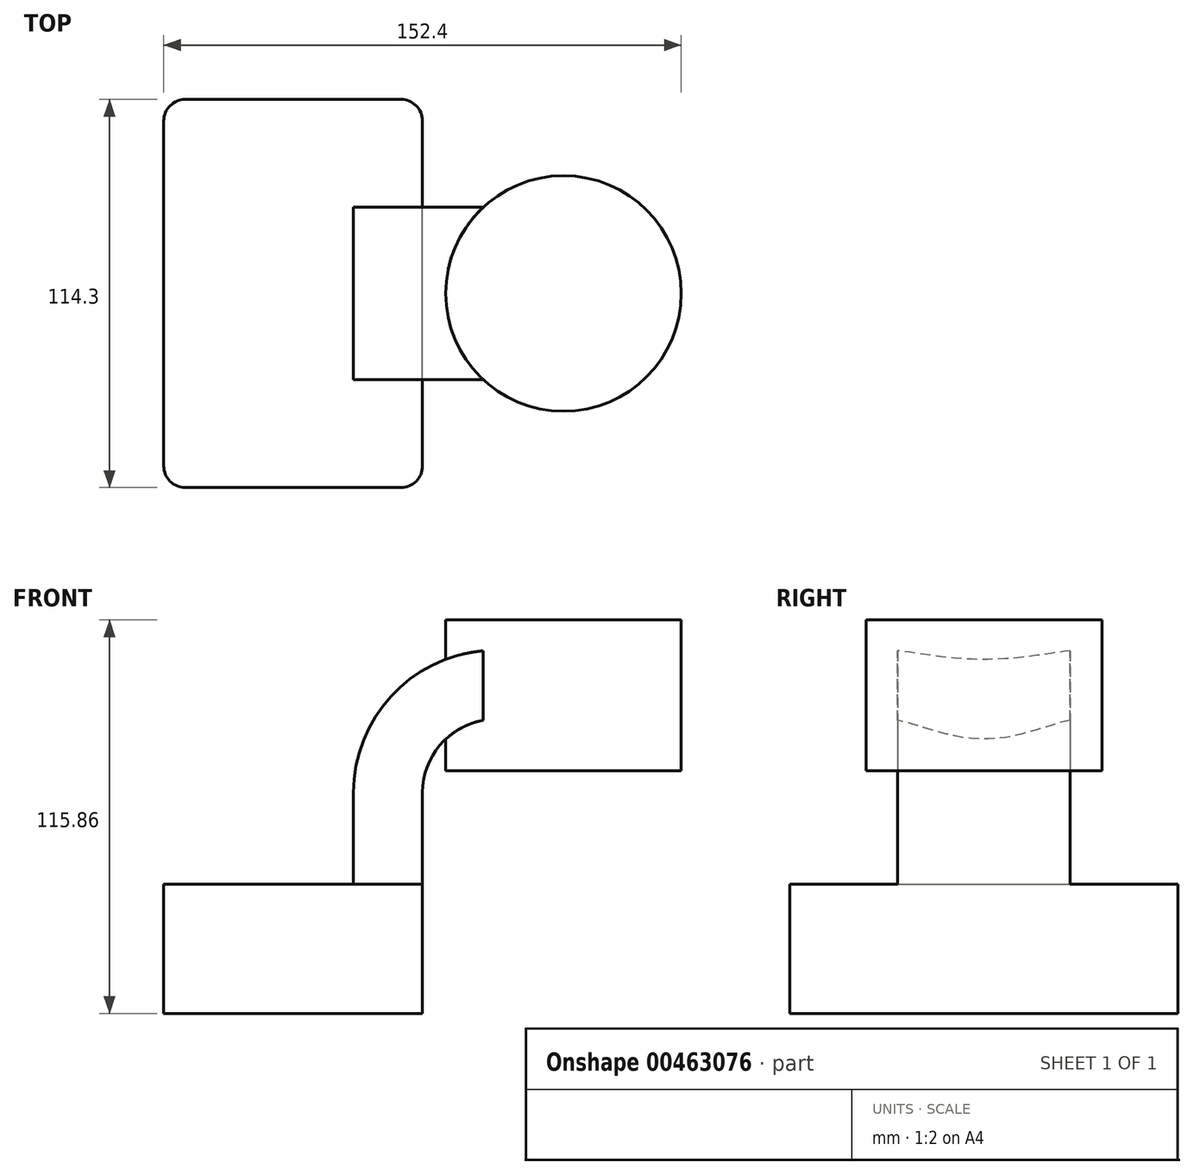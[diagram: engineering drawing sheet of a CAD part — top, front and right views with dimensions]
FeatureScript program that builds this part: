
annotation { "Feature Type Name" : "Feature", "Feature Type Description" : "" }
export const myFeature = defineFeature(function(context is Context, id is Id, definition is map)
    precondition{}
    {
        {
            var Q0;
            Q0=qCreatedBy(makeId("Front.planeOp"),FACE);
            var sketch = newSketch(context, id + "F0", { "sketchPlane" : qUnion([Q0])});
            skLineSegment(sketch, "E0.bottom", {"start": v(-34.93, -20.28) * mm, "end": v(41.27, -20.28) * mm});
            skLineSegment(sketch, "E0.top", {"start": v(-34.93, 17.82) * mm, "end": v(41.27, 17.82) * mm});
            skLineSegment(sketch, "E0.left", {"start": v(-34.93, -20.28) * mm, "end": v(-34.93, 17.82) * mm});
            skLineSegment(sketch, "E0.right", {"start": v(41.27, -20.28) * mm, "end": v(41.27, 17.82) * mm});
            skLineSegment(sketch, "E1", {"start": v(41.27, 17.82) * mm, "end": v(41.27, 44.74) * mm});
            skArc(sketch, "E2", {"start": v(41.27, 44.74) * mm, "mid": v(47.6, 60.01) * mm, "end": v(62.86, 66.33) * mm});
            skLineSegment(sketch, "E3", {"start": v(62.86, 66.33) * mm, "end": v(117.47, 66.33) * mm});
            skLineSegment(sketch, "E4.bottom", {"start": v(82.78, 95.58) * mm, "end": v(133.58, 95.58) * mm});
            skLineSegment(sketch, "E4.top", {"start": v(82.78, 51.13) * mm, "end": v(133.58, 51.13) * mm});
            skLineSegment(sketch, "E4.left", {"start": v(82.78, 95.58) * mm, "end": v(82.78, 51.13) * mm});
            skLineSegment(sketch, "E4.right", {"start": v(133.58, 95.58) * mm, "end": v(133.58, 51.13) * mm});
            skLineSegment(sketch, "E5.0", {"start": v(62.86, 86.65) * mm, "end": v(117.47, 86.65) * mm});
            skArc(sketch, "E5.1", {"start": v(20.95, 44.74) * mm, "mid": v(33.22, 74.38) * mm, "end": v(62.86, 86.65) * mm});
            skLineSegment(sketch, "E5.2", {"start": v(20.95, 17.82) * mm, "end": v(20.95, 44.74) * mm});
            skFitSpline(sketch, "E6", {"points": [v(82.78, 95.58) * mm, v(-34.93, 17.82) * mm], "startDerivative": vector(-171.54, -2.78) * mm, "endDerivative": vector(-60, -188.58) * mm});
            skLineSegment(sketch, "E7", {"start": v(117.47, 51.13) * mm, "end": v(117.47, 95.58) * mm});
            skSolve(sketch);
        }
        {
            var Q0;
            Q0=makeQuery(id+"F0.imprint","IMPRINT",FACE,{"disambiguationData":[TD([[makeQuery(id+"F0.imprint","IMPRINT",EDGE,{"derivedFrom":sQuery(id+"F0.wireOp",EDGE,"E0.bottom")}),1.0]])]});
            extrude(context, id + "F1", {"entities" : qUnion([Q0]), "endBound" : BoundingType.SYMMETRIC, "depth" : 114.3 * mm});
        }
        {
            var Q0;
            {var subQ5=sQuery(id+"F0.wireOp",EDGE,"E1");Q0=makeQuery(id+"F0.imprint","IMPRINT",FACE,{"disambiguationData":[TD([[makeQuery(id+"F0.imprint","IMPRINT",EDGE,{"derivedFrom":subQ5}),1.0]])]});}
            extrude(context, id + "F2", {"entities" : qUnion([Q0]), "operationType" : NewBodyOperationType.ADD, "endBound" : BoundingType.SYMMETRIC, "depth" : 50.8 * mm});
        }
        {
            var Q0;
            {var subQ0=sQuery(id+"F0.wireOp",EDGE,"E5.1");Q0=makeQuery(id+"F0.imprint","IMPRINT",FACE,{"disambiguationData":[TD([[makeQuery(id+"F0.imprint","IMPRINT",EDGE,{"derivedFrom":subQ0}),1.0]])]});}
            extrude(context, id + "F3", {"entities" : qUnion([Q0]), "operationType" : NewBodyOperationType.ADD, "endBound" : BoundingType.SYMMETRIC, "depth" : 25.4 * mm});
        }
        {
            var Q0;
            {var subQ3=sQuery(id+"F0.wireOp",EDGE,"E7");var subQ5=sQuery(id+"F0.wireOp",EDGE,"E5.0");var subQ6=makeQuery(id+"F0.imprint","INTERSECT",VERTEX,{"derivedFrom":[subQ5,subQ3]});Q0=makeQuery(id+"F0.imprint","IMPRINT",FACE,{"disambiguationData":[TD([[makeQuery(id+"F0.imprint","IMPRINT",EDGE,{"disambiguationData":[TD([[subQ6,1.0]])],"derivedFrom":subQ5}),1.0]])]});}
            var Q1;
            {var subQ0=sQuery(id+"F0.wireOp",EDGE,"E7");var subQ1=sQuery(id+"F0.wireOp",EDGE,"E3");var subQ2=makeQuery(id+"F0.imprint","INTERSECT",VERTEX,{"derivedFrom":[subQ1,subQ0]});Q1=makeQuery(id+"F0.imprint","IMPRINT",FACE,{"disambiguationData":[TD([[makeQuery(id+"F0.imprint","IMPRINT",EDGE,{"disambiguationData":[TD([[subQ2,1.0]])],"derivedFrom":subQ1}),1.0]])]});}
            var Q2;
            {var subQ0=sQuery(id+"F0.wireOp",EDGE,"E7");var subQ1=sQuery(id+"F0.wireOp",EDGE,"E3");var subQ2=makeQuery(id+"F0.imprint","INTERSECT",VERTEX,{"derivedFrom":[subQ1,subQ0]});Q2=makeQuery(id+"F0.imprint","IMPRINT",FACE,{"disambiguationData":[TD([[makeQuery(id+"F0.imprint","IMPRINT",EDGE,{"disambiguationData":[TD([[subQ2,1.0]])],"derivedFrom":subQ1}),-1.0]])]});}
            var Q3;
            Q3=sQuery(id+"F0.wireOp",EDGE,"E4.left");
            revolve(context, id + "F4", {"operationType" : NewBodyOperationType.ADD, "entities" : qUnion([Q0, Q1, Q2]), "axis" : qUnion([Q3]), "revolveType" : RevolveType.FULL});
        }
        {
            var Q0;
            Q0=makeQuery(id+"F1.opExtrude","CAP_EDGE",EDGE,{"disambiguationData":[OSD([sQuery(id+"F0.wireOp",EDGE,"E0.right")])],"isStart":true});
            var Q1;
            Q1=makeQuery(id+"F1.opExtrude","CAP_EDGE",EDGE,{"disambiguationData":[OSD([sQuery(id+"F0.wireOp",EDGE,"E0.left")])],"isStart":true});
            var Q2;
            Q2=makeQuery(id+"F1.opExtrude","CAP_EDGE",EDGE,{"disambiguationData":[OSD([sQuery(id+"F0.wireOp",EDGE,"E0.right")])],"isStart":false});
            var Q3;
            Q3=makeQuery(id+"F1.opExtrude","CAP_EDGE",EDGE,{"disambiguationData":[OSD([sQuery(id+"F0.wireOp",EDGE,"E0.left")])],"isStart":false});
            fillet(context, id + "F5", {"entities" : qUnion([Q0, Q1, Q2, Q3]), "radius" : 6.35 * mm, "tangentPropagation" : true, "allowEdgeOverflow" : false});
        }
    });
